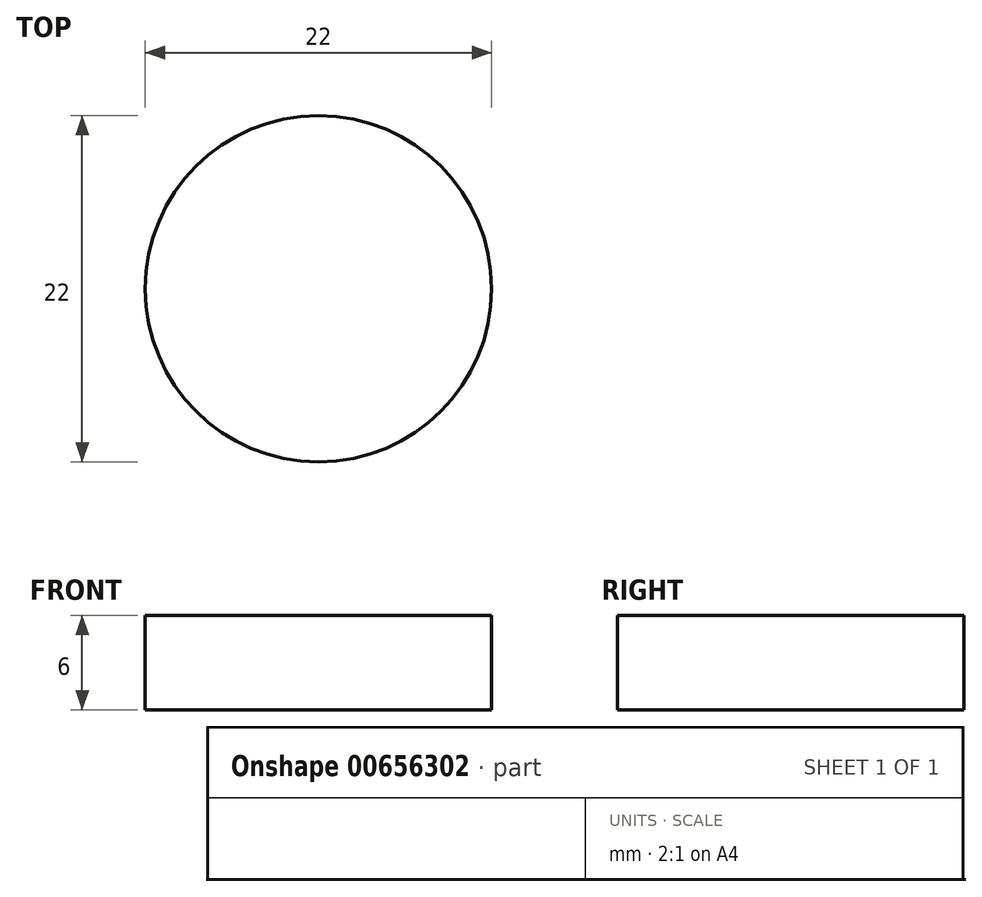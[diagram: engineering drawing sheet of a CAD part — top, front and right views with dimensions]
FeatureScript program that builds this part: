
annotation { "Feature Type Name" : "Feature", "Feature Type Description" : "" }
export const myFeature = defineFeature(function(context is Context, id is Id, definition is map)
    precondition{}
    {
        {
            var Q0;
            Q0=qCreatedBy(makeId("Top.planeOp"),FACE);
            var sketch = newSketch(context, id + "F0", { "sketchPlane" : qUnion([Q0])});
            skCircle(sketch, "E0", {"center": v(0, 0) * mm, "radius": 11 * mm});
            skSolve(sketch);
        }
        {
            var Q0;
            Q0=makeQuery(id+"F0.imprint","IMPRINT",FACE,{"disambiguationData":[TD([[makeQuery(id+"F0.imprint","IMPRINT",EDGE,{"derivedFrom":sQuery(id+"F0.wireOp",EDGE,"E0")}),1.0]])]});
            extrude(context, id + "F1", {"entities" : qUnion([Q0]), "depth" : 6 * mm, "offsetDistance" : 25 * mm});
        }
    });
